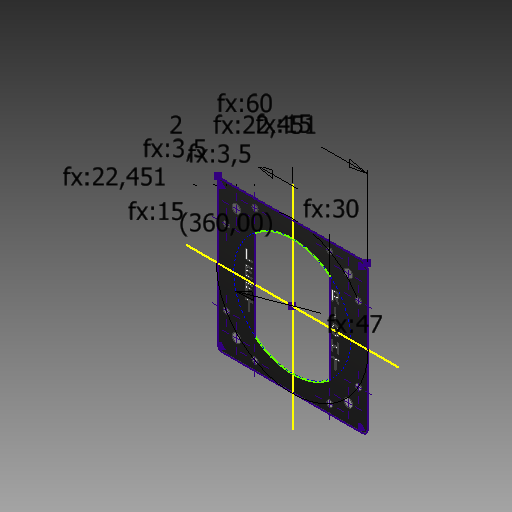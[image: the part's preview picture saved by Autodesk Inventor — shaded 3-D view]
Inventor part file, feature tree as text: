
AUTODESK INVENTOR PART (.ipt)
format: ipt  version: 2019 (Build 230136000, 136)  size: 334,336 bytes
history: native  units: mm
features: extrude x3, other x2, hole x2
ambient origin geometry x8: Origin, YZ Plane, XZ Plane, XY Plane, X Axis, Y Axis, Z Axis, Center Point
bodies: Solid1 (feature_tree)
feature tree (7):
  other  "FrontMask"
  other  "<userpath>\OneDrive - Van Ierland\Documents\Inventor\FlightSim\Instrument.xlsx"
  extrude  "Extrusion1"  Depth=60.0mm
  hole  "Hole1"  [1 undecoded]
  hole  "Hole2"  [1 undecoded]
  extrude  "Extrusion2"  Depth=22.45064mm
  extrude  "Extrusion3"  Depth=15.0mm
note: 2 required parameter values undecoded (feature->parameter linkage not recoverable at this tier; creation-order binding heuristic only, values carry confidence <= 0.55)
